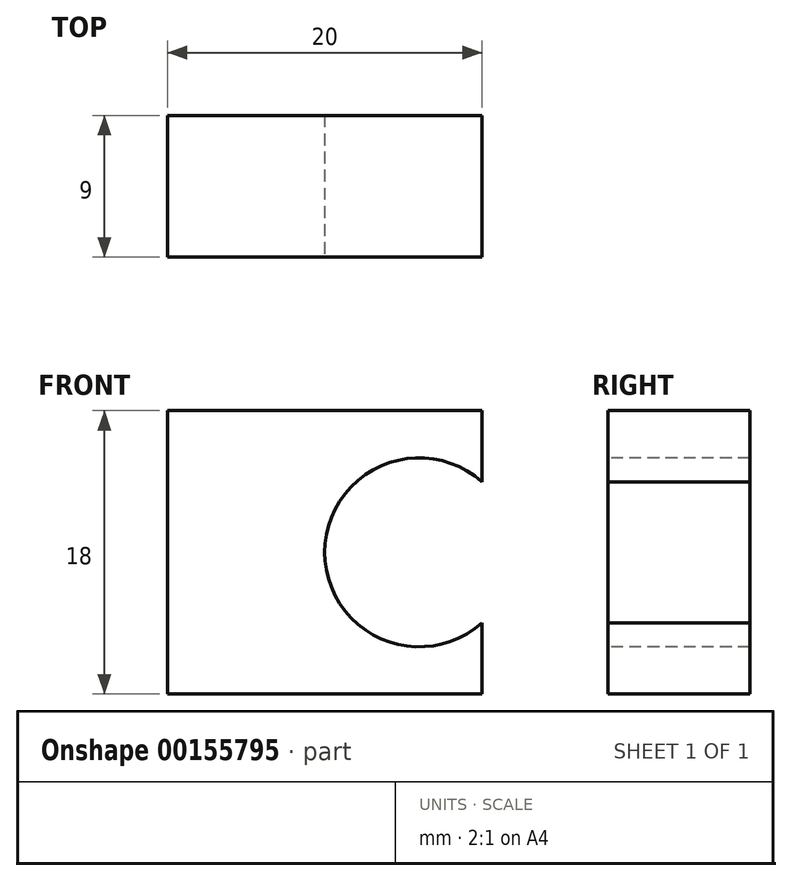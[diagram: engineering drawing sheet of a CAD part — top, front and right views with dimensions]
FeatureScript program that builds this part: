
annotation { "Feature Type Name" : "Feature", "Feature Type Description" : "" }
export const myFeature = defineFeature(function(context is Context, id is Id, definition is map)
    precondition{}
    {
        {
            var Q0;
            Q0=qCreatedBy(makeId("Right.planeOp"),FACE);
            var sketch = newSketch(context, id + "F0", { "sketchPlane" : qUnion([Q0])});
            skLineSegment(sketch, "E0", {"start": v(0, 37.95) * mm, "end": v(0, -36.16) * mm, "construction": true});
            skLineSegment(sketch, "E1", {"start": v(36.07, 0) * mm, "end": v(-36.79, 0) * mm, "construction": true});
            skLineSegment(sketch, "E2.bottom", {"start": v(4.5, -9) * mm, "end": v(-4.5, -9) * mm});
            skLineSegment(sketch, "E2.top", {"start": v(4.5, 9) * mm, "end": v(-4.5, 9) * mm});
            skLineSegment(sketch, "E2.left", {"start": v(4.5, -9) * mm, "end": v(4.5, 9) * mm});
            skLineSegment(sketch, "E2.right", {"start": v(-4.5, -9) * mm, "end": v(-4.5, 9) * mm});
            skPoint(sketch, "E2.middle", {"position": v(0, 0) * mm});
            skSolve(sketch);
        }
        {
            var Q0;
            Q0 = qSketchRegion(id + "F0", true);
            extrude(context, id + "F1", {"entities" : qUnion([Q0]), "depth" : 20 * mm, "offsetDistance" : 25 * mm});
        }
        {
            var Q0;
            Q0=makeQuery(id+"F1.opExtrude","SWEPT_FACE",FACE,{"disambiguationData":[OSD([sQuery(id+"F0.wireOp",EDGE,"E2.right")])]});
            var sketch = newSketch(context, id + "F2", { "sketchPlane" : qUnion([Q0])});
            skLineSegment(sketch, "E3", {"start": v(28.4, 0) * mm, "end": v(-11.62, 0) * mm, "construction": true});
            skLineSegment(sketch, "E4", {"start": v(16, 23.07) * mm, "end": v(16, -20.74) * mm, "construction": true});
            skCircle(sketch, "E5", {"center": v(16, 0) * mm, "radius": 6 * mm});
            skSolve(sketch);
        }
        {
            var Q0;
            Q0 = qSketchRegion(id + "F2", true);
            extrude(context, id + "F3", {"entities" : qUnion([Q0]), "operationType" : NewBodyOperationType.REMOVE, "oppositeDirection" : true, "depth" : 25 * mm});
        }
    });
